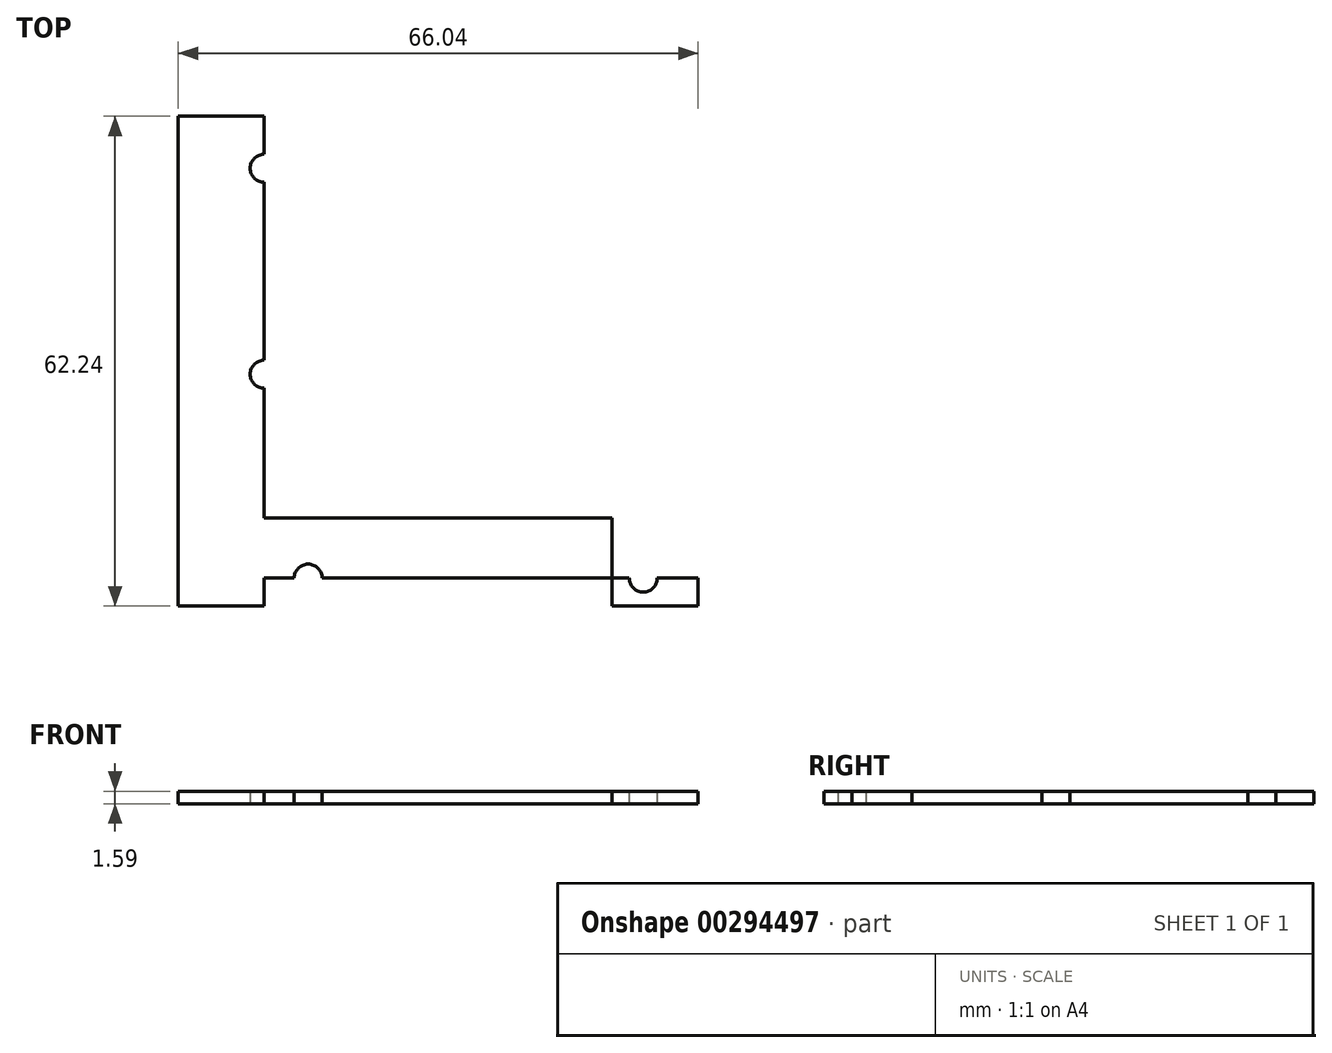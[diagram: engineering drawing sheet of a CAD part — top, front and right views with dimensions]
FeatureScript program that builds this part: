
annotation { "Feature Type Name" : "Feature", "Feature Type Description" : "" }
export const myFeature = defineFeature(function(context is Context, id is Id, definition is map)
    precondition{}
    {
        {
            var Q0;
            Q0=qCreatedBy(makeId("Top.planeOp"),FACE);
            var sketch = newSketch(context, id + "F0", { "sketchPlane" : qUnion([Q0])});
            skLineSegment(sketch, "E0.bottom", {"start": v(33.02, 31.12) * mm, "end": v(-33.02, 31.12) * mm});
            skLineSegment(sketch, "E0.top", {"start": v(33.02, -31.12) * mm, "end": v(-33.02, -31.12) * mm});
            skLineSegment(sketch, "E0.left", {"start": v(33.02, 31.12) * mm, "end": v(33.02, -31.12) * mm});
            skLineSegment(sketch, "E0.right", {"start": v(-33.02, 31.12) * mm, "end": v(-33.02, -31.12) * mm});
            skPoint(sketch, "E0.middle", {"position": v(0, 0) * mm});
            skLineSegment(sketch, "E1.bottom", {"start": v(22.1, 31.12) * mm, "end": v(-22.1, 31.12) * mm});
            skLineSegment(sketch, "E1.top", {"start": v(22.1, -31.12) * mm, "end": v(-22.1, -31.12) * mm});
            skLineSegment(sketch, "E1.left", {"start": v(22.1, 31.12) * mm, "end": v(22.1, -31.12) * mm});
            skLineSegment(sketch, "E1.right", {"start": v(-22.1, 31.12) * mm, "end": v(-22.1, -31.12) * mm});
            skCircle(sketch, "E2", {"center": v(22.1, 24.51) * mm, "radius": 1.78 * mm});
            skCircle(sketch, "E3", {"center": v(22.1, -1.65) * mm, "radius": 1.78 * mm});
            skCircle(sketch, "E4", {"center": v(-22.1, 24.51) * mm, "radius": 1.78 * mm});
            skCircle(sketch, "E5", {"center": v(-22.1, -1.65) * mm, "radius": 1.78 * mm});
            skLineSegment(sketch, "E6.bottom", {"start": v(-22.1, -9.78) * mm, "end": v(22.1, -9.78) * mm});
            skLineSegment(sketch, "E6.top", {"start": v(-22.1, -19.94) * mm, "end": v(22.1, -19.94) * mm});
            skLineSegment(sketch, "E6.left", {"start": v(-22.1, -9.78) * mm, "end": v(-22.1, -19.94) * mm});
            skLineSegment(sketch, "E6.right", {"start": v(22.1, -9.78) * mm, "end": v(22.1, -19.94) * mm});
            skLineSegment(sketch, "E7", {"start": v(-22.1, -27.56) * mm, "end": v(33.02, -27.56) * mm});
            skCircle(sketch, "E8", {"center": v(-16.51, -27.56) * mm, "radius": 1.78 * mm});
            skCircle(sketch, "E9", {"center": v(26.05, -27.56) * mm, "radius": 1.78 * mm});
            skSolve(sketch);
        }
        {
            var Q0;
            {var subQ9=sQuery(id+"F0.wireOp",EDGE,"E1.bottom");Q0=makeQuery(id+"F0.imprint","IMPRINT",FACE,{"disambiguationData":[TD([[makeQuery(id+"F0.imprint","IMPRINT",EDGE,{"derivedFrom":subQ9}),1.0]])]});}
            var Q1;
            {var subQ0=sQuery(id+"F0.wireOp",EDGE,"E0.right");Q1=makeQuery(id+"F0.imprint","IMPRINT",FACE,{"disambiguationData":[TD([[makeQuery(id+"F0.imprint","IMPRINT",EDGE,{"derivedFrom":subQ0}),1.0]])]});}
            var Q2;
            {var subQ6=sQuery(id+"F0.wireOp",EDGE,"E0.left");Q2=makeQuery(id+"F0.imprint","IMPRINT",FACE,{"disambiguationData":[TD([[makeQuery(id+"F0.imprint","IMPRINT",EDGE,{"derivedFrom":subQ6}),-1.0]])]});}
            var Q3;
            {var subQ5=sQuery(id+"F0.wireOp",EDGE,"E6.top");Q3=makeQuery(id+"F0.imprint","IMPRINT",FACE,{"disambiguationData":[TD([[makeQuery(id+"F0.imprint","IMPRINT",EDGE,{"derivedFrom":subQ5}),-1.0]])]});}
            var Q4;
            {var subQ1=sQuery(id+"F0.wireOp",EDGE,"E1.top");Q4=makeQuery(id+"F0.imprint","IMPRINT",FACE,{"disambiguationData":[TD([[makeQuery(id+"F0.imprint","IMPRINT",EDGE,{"derivedFrom":subQ1}),-1.0]])]});}
            var Q5;
            {var subQ5=sQuery(id+"F0.wireOp",EDGE,"E6.right");Q5=makeQuery(id+"F0.imprint","IMPRINT",FACE,{"disambiguationData":[TD([[makeQuery(id+"F0.imprint","IMPRINT",EDGE,{"derivedFrom":subQ5}),1.0]])]});}
            extrude(context, id + "F1", {"entities" : qUnion([Q0, Q1, Q2, Q3, Q4, Q5]), "depth" : 1.59 * mm});
        }
    });
